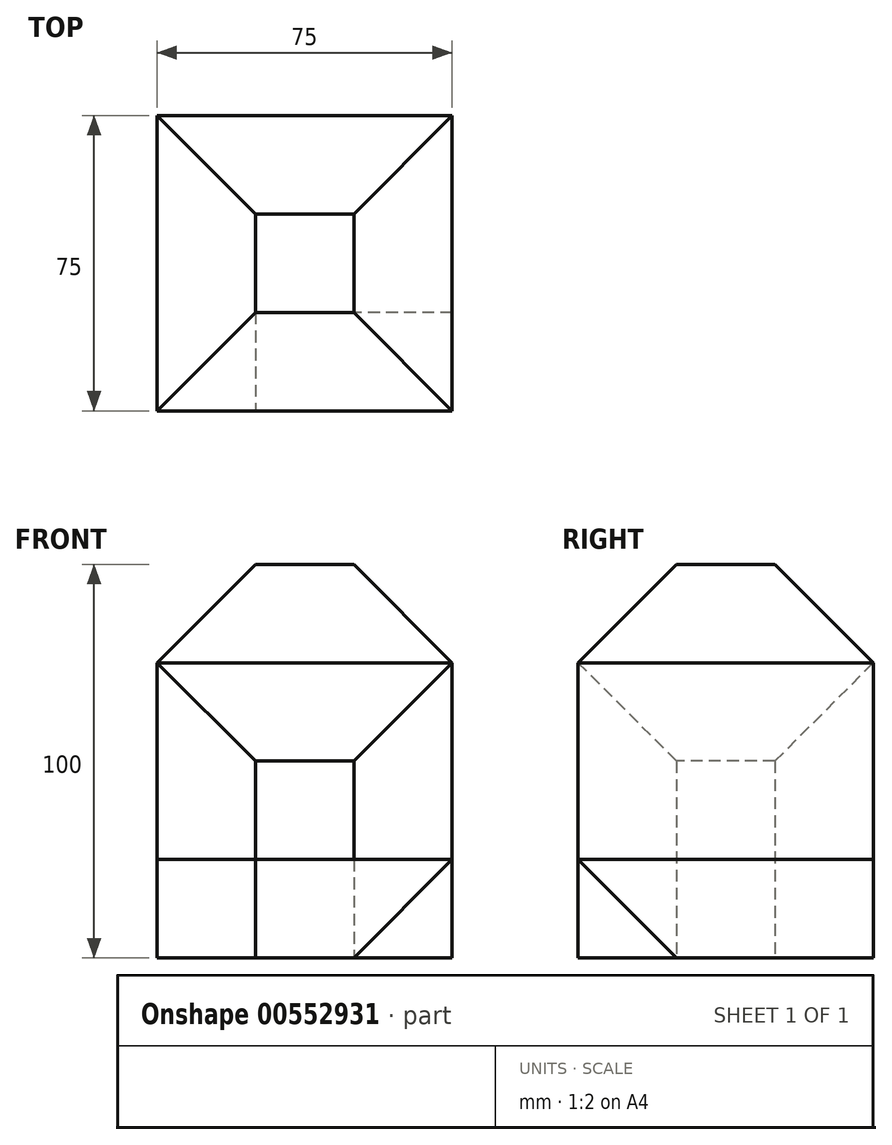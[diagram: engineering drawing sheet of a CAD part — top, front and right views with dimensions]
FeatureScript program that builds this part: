
annotation { "Feature Type Name" : "Feature", "Feature Type Description" : "" }
export const myFeature = defineFeature(function(context is Context, id is Id, definition is map)
    precondition{}
    {
        {
            var Q0;
            Q0=qCreatedBy(makeId("Top.planeOp"),FACE);
            var sketch = newSketch(context, id + "F0", { "sketchPlane" : qUnion([Q0])});
            skLineSegment(sketch, "E0.bottom", {"start": v(0, 0) * mm, "end": v(75, 0) * mm});
            skLineSegment(sketch, "E0.top", {"start": v(0, 75) * mm, "end": v(75, 75) * mm});
            skLineSegment(sketch, "E0.left", {"start": v(0, 0) * mm, "end": v(0, 75) * mm});
            skLineSegment(sketch, "E0.right", {"start": v(75, 0) * mm, "end": v(75, 75) * mm});
            skSolve(sketch);
        }
        {
            var Q0;
            Q0=qCreatedBy(makeId("Top.planeOp"),FACE);
            cPlane(context, id + "F1", {"entities" : qUnion([Q0]), "cplaneType" : CPlaneType.OFFSET, "offset" : 25 * mm, "width" : 150 * mm, "height" : 150 * mm});
        }
        {
            var Q0;
            Q0=qCreatedBy(id+"F1.planeOp",FACE);
            cPlane(context, id + "F2", {"entities" : qUnion([Q0]), "cplaneType" : CPlaneType.OFFSET, "offset" : 25 * mm, "width" : 150 * mm, "height" : 150 * mm});
        }
        {
            var Q0;
            Q0=qCreatedBy(id+"F2.planeOp",FACE);
            cPlane(context, id + "F3", {"entities" : qUnion([Q0]), "cplaneType" : CPlaneType.OFFSET, "offset" : 25 * mm, "width" : 150 * mm, "height" : 150 * mm});
        }
        {
            var Q0;
            Q0=qCreatedBy(id+"F3.planeOp",FACE);
            cPlane(context, id + "F4", {"entities" : qUnion([Q0]), "cplaneType" : CPlaneType.OFFSET, "offset" : 25 * mm, "width" : 150 * mm, "height" : 150 * mm});
        }
        {
            var Q0;
            Q0=qCreatedBy(id+"F3.planeOp",FACE);
            var sketch = newSketch(context, id + "F5", { "sketchPlane" : qUnion([Q0])});
            skLineSegment(sketch, "E1.bottom", {"start": v(0, 0) * mm, "end": v(75, 0) * mm});
            skLineSegment(sketch, "E1.top", {"start": v(0, 75) * mm, "end": v(75, 75) * mm});
            skLineSegment(sketch, "E1.left", {"start": v(0, 0) * mm, "end": v(0, 75) * mm});
            skLineSegment(sketch, "E1.right", {"start": v(75, 0) * mm, "end": v(75, 75) * mm});
            skSolve(sketch);
        }
        {
            var Q0;
            Q0=qCreatedBy(id+"F4.planeOp",FACE);
            var sketch = newSketch(context, id + "F6", { "sketchPlane" : qUnion([Q0])});
            skLineSegment(sketch, "E2.bottom", {"start": v(25, 25) * mm, "end": v(50, 25) * mm});
            skLineSegment(sketch, "E2.top", {"start": v(25, 50) * mm, "end": v(50, 50) * mm});
            skLineSegment(sketch, "E2.left", {"start": v(25, 25) * mm, "end": v(25, 50) * mm});
            skLineSegment(sketch, "E2.right", {"start": v(50, 25) * mm, "end": v(50, 50) * mm});
            skSolve(sketch);
        }
        {
            var Q0;
            Q0=makeQuery(id+"F5.imprint","IMPRINT",FACE,{"disambiguationData":[TD([[makeQuery(id+"F5.imprint","IMPRINT",EDGE,{"derivedFrom":sQuery(id+"F5.wireOp",EDGE,"E1.bottom")}),1.0]])]});
            var Q1;
            Q1=makeQuery(id+"F6.imprint","IMPRINT",FACE,{"disambiguationData":[TD([[makeQuery(id+"F6.imprint","IMPRINT",EDGE,{"derivedFrom":sQuery(id+"F6.wireOp",EDGE,"E2.bottom")}),1.0]])]});
            loft(context, id + "F7", {"sheetProfilesArray" : [{ "sheetProfileEntities" : qUnion([Q0]) }, { "sheetProfileEntities" : qUnion([Q1]) }]});
        }
        {
            var Q0;
            Q0=qCreatedBy(id+"F2.planeOp",FACE);
            var sketch = newSketch(context, id + "F8", { "sketchPlane" : qUnion([Q0])});
            skLineSegment(sketch, "E3.0.0", {"start": v(50, 50) * mm, "end": v(25, 50) * mm});
            skLineSegment(sketch, "E3.0.1", {"start": v(25, 50) * mm, "end": v(25, 25) * mm});
            skLineSegment(sketch, "E3.0.2", {"start": v(25, 25) * mm, "end": v(50, 25) * mm});
            skLineSegment(sketch, "E3.0.3", {"start": v(50, 25) * mm, "end": v(50, 50) * mm});
            skSolve(sketch);
        }
        {
            var Q1;
            Q1 = qSketchRegion(id + "F5", true);
            var Q2;
            Q2 = qSketchRegion(id + "F8", true);
            loft(context, id + "F9", {"sheetProfilesArray" : [{ "sheetProfileEntities" : qUnion([Q1]) }, { "sheetProfileEntities" : qUnion([Q2]) }]});
        }
        {
            var Q0;
            Q0=qCreatedBy(makeId("Top.planeOp"),FACE);
            var sketch = newSketch(context, id + "F10", { "sketchPlane" : qUnion([Q0])});
            skLineSegment(sketch, "E4.0", {"start": v(75, 0) * mm, "end": v(75, 75) * mm});
            skLineSegment(sketch, "E4.1", {"start": v(75, 75) * mm, "end": v(50, 50) * mm});
            skLineSegment(sketch, "E4.2", {"start": v(50, 50) * mm, "end": v(50, 25) * mm});
            skLineSegment(sketch, "E4.3", {"start": v(75, 0) * mm, "end": v(50, 25) * mm});
            skSolve(sketch);
        }
        {
            var Q0;
            Q0=makeQuery(id+"F10.imprint","IMPRINT",FACE,{"disambiguationData":[TD([[makeQuery(id+"F10.imprint","IMPRINT",EDGE,{"derivedFrom":sQuery(id+"F10.wireOp",EDGE,"E4.0")}),1.0]])]});
            var Q1;
            Q1=makeQuery(id+"F9.opLoft","SWEPT_FACE",FACE,{"disambiguationData":[OSD([sQuery(id+"F5.wireOp",EDGE,"E1.bottom"),sQuery(id+"F5.wireOp",EDGE,"E1.top"),sQuery(id+"F5.wireOp",EDGE,"E1.right"),sQuery(id+"F8.wireOp",EDGE,"E3.0.0"),sQuery(id+"F8.wireOp",EDGE,"E3.0.2"),sQuery(id+"F8.wireOp",EDGE,"E3.0.3")])]});
            extrude(context, id + "F11", {"entities" : qUnion([Q0]), "operationType" : NewBodyOperationType.ADD, "endBound" : BoundingType.UP_TO_SURFACE, "depth" : 25 * mm, "endBoundEntityFace" : qUnion([Q1]), "offsetDistance" : 25 * mm});
        }
        {
            var Q0;
            Q0=qCreatedBy(makeId("Top.planeOp"),FACE);
            var sketch = newSketch(context, id + "F12", { "sketchPlane" : qUnion([Q0])});
            skLineSegment(sketch, "E5.0", {"start": v(0, 75) * mm, "end": v(25, 50) * mm});
            skLineSegment(sketch, "E6.0", {"start": v(25, 25) * mm, "end": v(25, 50) * mm});
            skLineSegment(sketch, "E7.0.2", {"start": v(25, 25) * mm, "end": v(0, 0) * mm});
            skLineSegment(sketch, "E7.0.3", {"start": v(0, 0) * mm, "end": v(0, 75) * mm});
            skSolve(sketch);
        }
        {
            var Q0;
            Q0 = qSketchRegion(id + "F12", true);
            var Q1;
            Q1=makeQuery(id+"F9.opLoft","SWEPT_FACE",FACE,{"disambiguationData":[OSD([sQuery(id+"F5.wireOp",EDGE,"E1.bottom"),sQuery(id+"F5.wireOp",EDGE,"E1.top"),sQuery(id+"F5.wireOp",EDGE,"E1.left"),sQuery(id+"F8.wireOp",EDGE,"E3.0.0"),sQuery(id+"F8.wireOp",EDGE,"E3.0.1"),sQuery(id+"F8.wireOp",EDGE,"E3.0.2")])]});
            extrude(context, id + "F13", {"entities" : qUnion([Q0]), "endBound" : BoundingType.UP_TO_SURFACE, "depth" : 25 * mm, "endBoundEntityFace" : qUnion([Q1]), "offsetDistance" : 25 * mm});
        }
        {
            var Q0;
            Q0 = qSketchRegion(id + "F0", true);
            extrude(context, id + "F14", {"entities" : qUnion([Q0]), "depth" : 25 * mm, "offsetDistance" : 25 * mm});
        }
        {
            var Q0;
            Q0=qCreatedBy(makeId("Right.planeOp"),FACE);
            var sketch = newSketch(context, id + "F15", { "sketchPlane" : qUnion([Q0])});
            skLineSegment(sketch, "E8", {"start": v(0, 25) * mm, "end": v(25, 0) * mm});
            skLineSegment(sketch, "E9", {"start": v(25, 0) * mm, "end": v(0, 0) * mm});
            skLineSegment(sketch, "E10", {"start": v(0, 0) * mm, "end": v(0, 25) * mm});
            skSolve(sketch);
        }
        {
            var Q0;
            Q0 = qSketchRegion(id + "F15", true);
            extrude(context, id + "F16", {"entities" : qUnion([Q0]), "operationType" : NewBodyOperationType.REMOVE, "depth" : 75 * mm, "offsetDistance" : 25 * mm, "hasSecondDirection" : true, "secondDirectionOppositeDirection" : true, "secondDirectionDepth" : -25 * mm});
        }
    });
